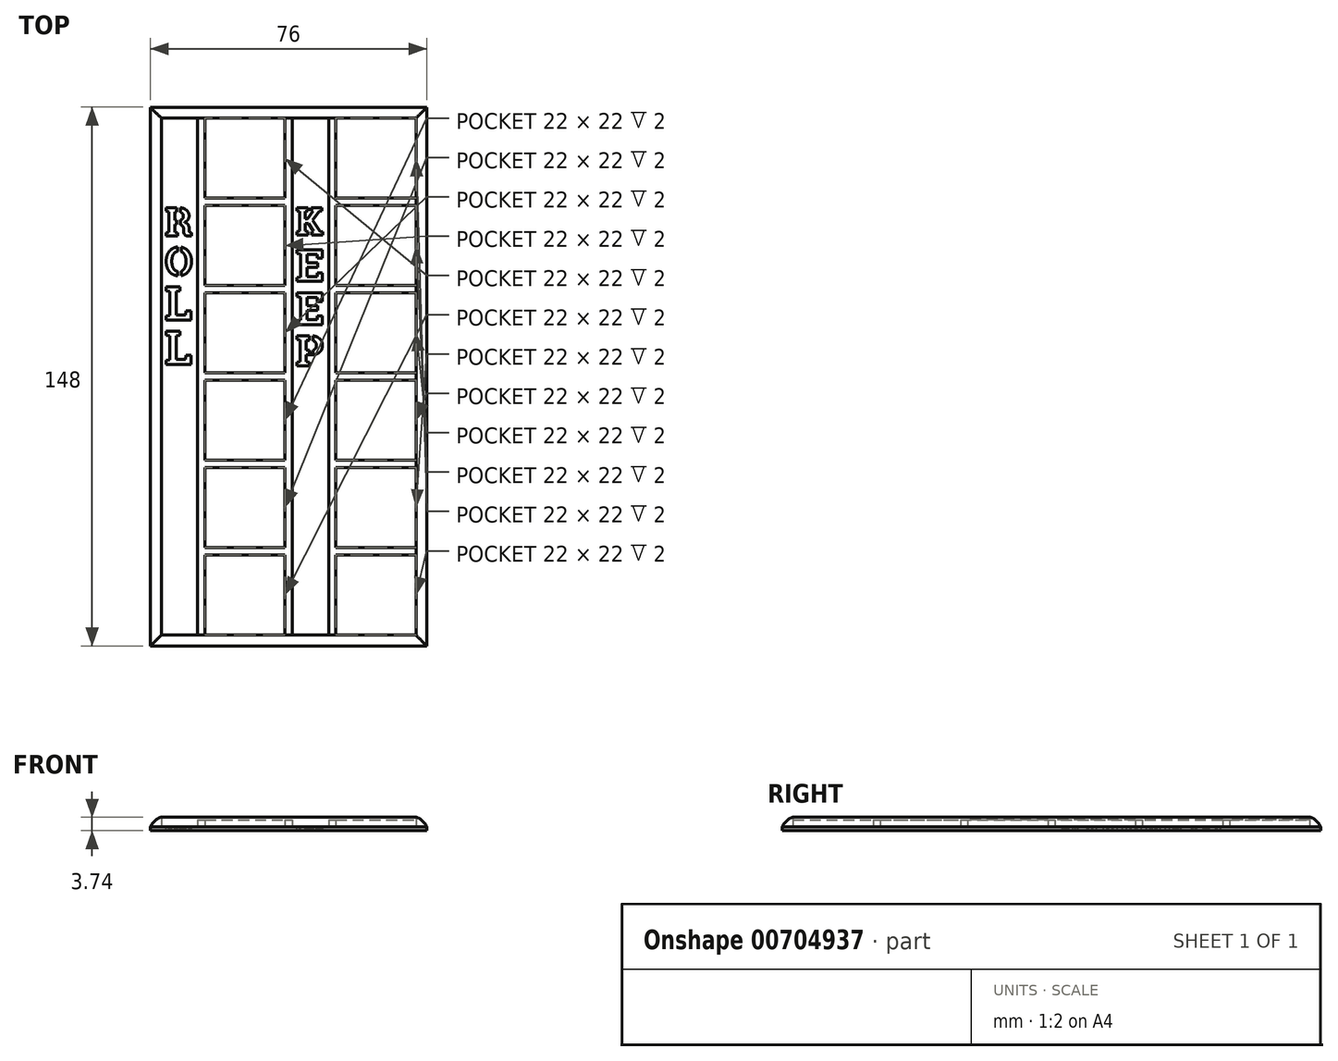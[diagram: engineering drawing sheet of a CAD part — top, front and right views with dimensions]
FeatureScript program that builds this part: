
annotation { "Feature Type Name" : "Feature", "Feature Type Description" : "" }
export const myFeature = defineFeature(function(context is Context, id is Id, definition is map)
    precondition{}
    {
        {
            var Q0;
            Q0=qCreatedBy(makeId("Top.planeOp"),FACE);
            var sketch = newSketch(context, id + "F0", { "sketchPlane" : qUnion([Q0])});
            skLineSegment(sketch, "E0.bottom", {"start": v(-38, 75.1) * mm, "end": v(38, 75.1) * mm});
            skLineSegment(sketch, "E0.top", {"start": v(-38, -72.9) * mm, "end": v(38, -72.9) * mm});
            skLineSegment(sketch, "E0.left", {"start": v(-38, 75.1) * mm, "end": v(-38, -72.9) * mm});
            skLineSegment(sketch, "E0.right", {"start": v(38, 75.1) * mm, "end": v(38, -72.9) * mm});
            skLineSegment(sketch, "E1.left", {"start": v(11, -69.9) * mm, "end": v(11, 72.1) * mm});
            skLineSegment(sketch, "E1.right", {"start": v(-35, -69.9) * mm, "end": v(-35, 72.1) * mm});
            skLineSegment(sketch, "E2", {"start": v(-25, 72.1) * mm, "end": v(-25, -69.9) * mm});
            skLineSegment(sketch, "E3.1.0.0", {"start": v(-1, 72.1) * mm, "end": v(-1, -69.9) * mm});
            skLineSegment(sketch, "E3.2.0.0", {"start": v(13, 72.1) * mm, "end": v(13, -69.9) * mm});
            skLineSegment(sketch, "E4", {"start": v(-23, -69.9) * mm, "end": v(-23, 72.1) * mm});
            skLineSegment(sketch, "E5.1.0.0", {"start": v(1, -69.9) * mm, "end": v(1, 72.1) * mm});
            skLineSegment(sketch, "E5.2.0.0", {"start": v(35, -69.9) * mm, "end": v(35, 72.1) * mm});
            skLineSegment(sketch, "E6", {"start": v(-35, 72.1) * mm, "end": v(35, 72.1) * mm});
            skLineSegment(sketch, "E7", {"start": v(35, -69.9) * mm, "end": v(-35, -69.9) * mm});
            skLineSegment(sketch, "E8.bottom", {"start": v(-29.5, 28.1) * mm, "end": v(-30.5, 28.1) * mm});
            skLineSegment(sketch, "E8.top", {"start": v(-29.5, 38.1) * mm, "end": v(-30.5, 38.1) * mm});
            skLineSegment(sketch, "E8.left", {"start": v(-29.5, 28.1) * mm, "end": v(-29.5, 38.1) * mm});
            skLineSegment(sketch, "E8.right", {"start": v(-30.5, 28.1) * mm, "end": v(-30.5, 38.1) * mm});
            skLineSegment(sketch, "E9.bottom", {"start": v(-30.75, 52.1) * mm, "end": v(-29.75, 52.1) * mm});
            skLineSegment(sketch, "E9.top", {"start": v(-30.75, 42.1) * mm, "end": v(-29.75, 42.1) * mm});
            skLineSegment(sketch, "E9.left", {"start": v(-30.75, 52.1) * mm, "end": v(-30.75, 42.1) * mm});
            skLineSegment(sketch, "E9.right", {"start": v(-29.75, 52.1) * mm, "end": v(-29.75, 42.1) * mm});
            skLineSegment(sketch, "E10.bottom", {"start": v(5.75, 7.6) * mm, "end": v(6.75, 7.6) * mm});
            skLineSegment(sketch, "E10.top", {"start": v(5.75, 13.6) * mm, "end": v(6.75, 13.6) * mm});
            skLineSegment(sketch, "E10.left", {"start": v(5.75, 7.6) * mm, "end": v(5.75, 13.6) * mm});
            skLineSegment(sketch, "E10.right", {"start": v(6.75, 7.6) * mm, "end": v(6.75, 13.6) * mm});
            skSolve(sketch);
        }
        {
            var Q0;
            Q0=qCreatedBy(makeId("Top.planeOp"),FACE);
            var sketch = newSketch(context, id + "F1", { "sketchPlane" : qUnion([Q0])});
            skLineSegment(sketch, "E11", {"start": v(-25, 72.1) * mm, "end": v(-25, -69.9) * mm});
            skLineSegment(sketch, "E12", {"start": v(-35, -69.9) * mm, "end": v(-35, 72.1) * mm});
            skLineSegment(sketch, "E13", {"start": v(11, -69.9) * mm, "end": v(11, 72.1) * mm});
            skLineSegment(sketch, "E14", {"start": v(13, 72.1) * mm, "end": v(13, -69.9) * mm});
            skLineSegment(sketch, "E15", {"start": v(-23, 72.1) * mm, "end": v(-1, 72.1) * mm});
            skLineSegment(sketch, "E16", {"start": v(-23, -69.9) * mm, "end": v(-23, 72.1) * mm});
            skLineSegment(sketch, "E17", {"start": v(-1, -69.9) * mm, "end": v(-23, -69.9) * mm});
            skLineSegment(sketch, "E18", {"start": v(-1, 72.1) * mm, "end": v(-1, -69.9) * mm});
            skLineSegment(sketch, "E19", {"start": v(-25, 72.1) * mm, "end": v(-23, 72.1) * mm});
            skLineSegment(sketch, "E20", {"start": v(-23, -69.9) * mm, "end": v(-25, -69.9) * mm});
            skLineSegment(sketch, "E21.bottom", {"start": v(-23, 50.1) * mm, "end": v(-1, 50.1) * mm});
            skLineSegment(sketch, "E21.top", {"start": v(-23, 48.1) * mm, "end": v(-1, 48.1) * mm});
            skLineSegment(sketch, "E21.left", {"start": v(-23, 50.1) * mm, "end": v(-23, 48.1) * mm});
            skLineSegment(sketch, "E21.right", {"start": v(-1, 50.1) * mm, "end": v(-1, 48.1) * mm});
            skLineSegment(sketch, "E22.bottom", {"start": v(-23, 26.1) * mm, "end": v(-1, 26.1) * mm});
            skLineSegment(sketch, "E22.top", {"start": v(-23, 24.1) * mm, "end": v(-1, 24.1) * mm});
            skLineSegment(sketch, "E23.bottom", {"start": v(-23, 2.1) * mm, "end": v(-1, 2.1) * mm});
            skLineSegment(sketch, "E23.top", {"start": v(-23, 0.1) * mm, "end": v(-1, 0.1) * mm});
            skLineSegment(sketch, "E24.bottom", {"start": v(-23, -21.9) * mm, "end": v(-1, -21.9) * mm});
            skLineSegment(sketch, "E24.top", {"start": v(-23, -23.9) * mm, "end": v(-1, -23.9) * mm});
            skLineSegment(sketch, "E25.bottom", {"start": v(-23, -45.9) * mm, "end": v(-1, -45.9) * mm});
            skLineSegment(sketch, "E25.top", {"start": v(-23, -47.9) * mm, "end": v(-1, -47.9) * mm});
            skLineSegment(sketch, "E26.bottom", {"start": v(13, 50.1) * mm, "end": v(35, 50.1) * mm});
            skLineSegment(sketch, "E26.top", {"start": v(13, 48.1) * mm, "end": v(35, 48.1) * mm});
            skLineSegment(sketch, "E27.bottom", {"start": v(13, 26.1) * mm, "end": v(35, 26.1) * mm});
            skLineSegment(sketch, "E27.top", {"start": v(13, 24.1) * mm, "end": v(35, 24.1) * mm});
            skLineSegment(sketch, "E28.bottom", {"start": v(13, 2.1) * mm, "end": v(35, 2.1) * mm});
            skLineSegment(sketch, "E28.top", {"start": v(13, 0.1) * mm, "end": v(35, 0.1) * mm});
            skLineSegment(sketch, "E29.bottom", {"start": v(13, -21.9) * mm, "end": v(35, -21.9) * mm});
            skLineSegment(sketch, "E29.top", {"start": v(13, -23.9) * mm, "end": v(35, -23.9) * mm});
            skLineSegment(sketch, "E30.bottom", {"start": v(13, -45.9) * mm, "end": v(35, -45.9) * mm});
            skLineSegment(sketch, "E30.top", {"start": v(13, -47.9) * mm, "end": v(35, -47.9) * mm});
            skLineSegment(sketch, "E31", {"start": v(13, -69.9) * mm, "end": v(11, -69.9) * mm});
            skLineSegment(sketch, "E32", {"start": v(11, 72.1) * mm, "end": v(13, 72.1) * mm});
            skLineSegment(sketch, "E33", {"start": v(35, -69.9) * mm, "end": v(13, -69.9) * mm});
            skLineSegment(sketch, "E34", {"start": v(35, -69.9) * mm, "end": v(35, 72.1) * mm});
            skLineSegment(sketch, "E35", {"start": v(13, 72.1) * mm, "end": v(35, 72.1) * mm});
            skSolve(sketch);
        }
        {
            var Q0;
            Q0=makeQuery(id+"F0.imprint","IMPRINT",FACE,{"disambiguationData":[TD([[makeQuery(id+"F0.imprint","IMPRINT",EDGE,{"derivedFrom":sQuery(id+"F0.wireOp",EDGE,"E0.bottom")}),-1.0]])]});
            var Q1;
            Q1=sQuery(id+"F0.wireOp",EDGE,"E1.top");
            var Q2;
            Q2=sQuery(id+"F1.wireOp",EDGE,"1024a238-9103-462a-9477-26902ec0aa7303");
            var Q3;
            Q3=sQuery(id+"F0.wireOp",EDGE,"E0.bottom");
            var Q4;
            Q4=sQuery(id+"F0.wireOp",EDGE,"E1.right");
            var Q5;
            Q5=sQuery(id+"F0.wireOp",EDGE,"E0.left");
            var Q6;
            Q6=sQuery(id+"F0.wireOp",EDGE,"E0.top");
            var Q7;
            Q7=sQuery(id+"F0.wireOp",EDGE,"E1.bottom");
            var Q8;
            Q8=sQuery(id+"F1.wireOp",EDGE,"1024a238-9103-462a-9477-26902ec0aa7301");
            var Q9;
            Q9=sQuery(id+"F0.wireOp",EDGE,"E1.left");
            var Q10;
            Q10=sQuery(id+"F0.wireOp",EDGE,"E0.right");
            extrude(context, id + "F2", {"entities" : qUnion([Q0]), "surfaceEntities" : qUnion([Q1, Q2, Q3, Q4, Q5, Q6, Q7, Q8, Q9, Q10]), "depth" : 3 * mm, "offsetDistance" : 25 * mm});
        }
        {
            var Q0;
            {var subQ0=sQuery(id+"F0.wireOp",EDGE,"E2");Q0=makeQuery(id+"F0.imprint","IMPRINT",FACE,{"disambiguationData":[TD([[makeQuery(id+"F0.imprint","IMPRINT",EDGE,{"derivedFrom":subQ0}),1.0]])]});}
            var Q1;
            {var subQ0=sQuery(id+"F0.wireOp",EDGE,"E3.1.0.0");Q1=makeQuery(id+"F0.imprint","IMPRINT",FACE,{"disambiguationData":[TD([[makeQuery(id+"F0.imprint","IMPRINT",EDGE,{"derivedFrom":subQ0}),1.0]])]});}
            var Q2;
            {var subQ0=sQuery(id+"F0.wireOp",EDGE,"E1.left");Q2=makeQuery(id+"F0.imprint","IMPRINT",FACE,{"disambiguationData":[TD([[makeQuery(id+"F0.imprint","IMPRINT",EDGE,{"derivedFrom":subQ0}),-1.0]])]});}
            var Q3;
            Q3=sQuery(id+"F0.wireOp",EDGE,"E2");
            var Q4;
            Q4=sQuery(id+"F0.wireOp",EDGE,"E4");
            extrude(context, id + "F3", {"entities" : qUnion([Q0, Q1, Q2]), "operationType" : NewBodyOperationType.ADD, "surfaceEntities" : qUnion([Q3, Q4]), "depth" : 2 * mm, "offsetDistance" : 25 * mm});
        }
        {
            var Q0;
            Q0=makeQuery(id+"F2.opExtrude","CAP_EDGE",EDGE,{"disambiguationData":[OSD([sQuery(id+"F0.wireOp",EDGE,"E0.right")])],"isStart":false});
            var Q1;
            Q1=makeQuery(id+"F2.opExtrude","CAP_EDGE",EDGE,{"disambiguationData":[OSD([sQuery(id+"F0.wireOp",EDGE,"E0.top")])],"isStart":false});
            var Q2;
            Q2=makeQuery(id+"F2.opExtrude","CAP_EDGE",EDGE,{"disambiguationData":[OSD([sQuery(id+"F0.wireOp",EDGE,"E0.left")])],"isStart":false});
            var Q3;
            Q3=makeQuery(id+"F2.opExtrude","CAP_EDGE",EDGE,{"disambiguationData":[OSD([sQuery(id+"F0.wireOp",EDGE,"E0.bottom")])],"isStart":false});
            fillet(context, id + "F4", {"entities" : qUnion([Q0, Q1, Q2, Q3]), "radius" : 5 * mm, "tangentPropagation" : true, "allowEdgeOverflow" : false});
        }
        {
            var Q0;
            Q0=qCreatedBy(makeId("Top.planeOp"),FACE);
            var sketch = newSketch(context, id + "F5", { "sketchPlane" : qUnion([Q0])});
            skLineSegment(sketch, "E36.bottom", {"start": v(-38, -72.9) * mm, "end": v(38, -72.9) * mm});
            skLineSegment(sketch, "E36.top", {"start": v(-38, 75.1) * mm, "end": v(38, 75.1) * mm});
            skLineSegment(sketch, "E36.left", {"start": v(-38, -72.9) * mm, "end": v(-38, 75.1) * mm});
            skLineSegment(sketch, "E36.right", {"start": v(38, -72.9) * mm, "end": v(38, 75.1) * mm});
            skSolve(sketch);
        }
        {
            var Q0;
            {var subQ0=sQuery(id+"F1.wireOp",EDGE,"E26.bottom");Q0=makeQuery(id+"F1.imprint","IMPRINT",FACE,{"disambiguationData":[TD([[makeQuery(id+"F1.imprint","IMPRINT",EDGE,{"derivedFrom":subQ0}),-1.0]])]});}
            var Q1;
            {var subQ0=sQuery(id+"F1.wireOp",EDGE,"E27.bottom");Q1=makeQuery(id+"F1.imprint","IMPRINT",FACE,{"disambiguationData":[TD([[makeQuery(id+"F1.imprint","IMPRINT",EDGE,{"derivedFrom":subQ0}),-1.0]])]});}
            var Q2;
            {var subQ0=sQuery(id+"F1.wireOp",EDGE,"E28.bottom");Q2=makeQuery(id+"F1.imprint","IMPRINT",FACE,{"disambiguationData":[TD([[makeQuery(id+"F1.imprint","IMPRINT",EDGE,{"derivedFrom":subQ0}),-1.0]])]});}
            var Q3;
            {var subQ0=sQuery(id+"F1.wireOp",EDGE,"E29.bottom");Q3=makeQuery(id+"F1.imprint","IMPRINT",FACE,{"disambiguationData":[TD([[makeQuery(id+"F1.imprint","IMPRINT",EDGE,{"derivedFrom":subQ0}),-1.0]])]});}
            var Q4;
            {var subQ0=sQuery(id+"F1.wireOp",EDGE,"E30.bottom");Q4=makeQuery(id+"F1.imprint","IMPRINT",FACE,{"disambiguationData":[TD([[makeQuery(id+"F1.imprint","IMPRINT",EDGE,{"derivedFrom":subQ0}),-1.0]])]});}
            var Q5;
            {var subQ0=sQuery(id+"F1.wireOp",EDGE,"E25.bottom");Q5=makeQuery(id+"F1.imprint","IMPRINT",FACE,{"disambiguationData":[TD([[makeQuery(id+"F1.imprint","IMPRINT",EDGE,{"derivedFrom":subQ0}),-1.0]])]});}
            var Q6;
            {var subQ0=sQuery(id+"F1.wireOp",EDGE,"E24.bottom");Q6=makeQuery(id+"F1.imprint","IMPRINT",FACE,{"disambiguationData":[TD([[makeQuery(id+"F1.imprint","IMPRINT",EDGE,{"derivedFrom":subQ0}),-1.0]])]});}
            var Q7;
            {var subQ0=sQuery(id+"F1.wireOp",EDGE,"E23.bottom");Q7=makeQuery(id+"F1.imprint","IMPRINT",FACE,{"disambiguationData":[TD([[makeQuery(id+"F1.imprint","IMPRINT",EDGE,{"derivedFrom":subQ0}),-1.0]])]});}
            var Q8;
            {var subQ0=sQuery(id+"F1.wireOp",EDGE,"E22.bottom");Q8=makeQuery(id+"F1.imprint","IMPRINT",FACE,{"disambiguationData":[TD([[makeQuery(id+"F1.imprint","IMPRINT",EDGE,{"derivedFrom":subQ0}),-1.0]])]});}
            var Q9;
            Q9=makeQuery(id+"F1.imprint","IMPRINT",FACE,{"disambiguationData":[TD([[makeQuery(id+"F1.imprint","IMPRINT",EDGE,{"derivedFrom":sQuery(id+"F1.wireOp",EDGE,"E21.bottom")}),-1.0]])]});
            extrude(context, id + "F6", {"entities" : qUnion([Q0, Q1, Q2, Q3, Q4, Q5, Q6, Q7, Q8, Q9]), "operationType" : NewBodyOperationType.ADD, "depth" : 2 * mm, "offsetDistance" : 25 * mm});
        }
        {
            var Q0;
            Q0=qCreatedBy(makeId("Top.planeOp"),FACE);
            var sketch = newSketch(context, id + "F7", { "sketchPlane" : qUnion([Q0])});
            skText(sketch, "E37", { "text": "R", "fontName": "RobotoSlab-Bold.ttf"});
            const initialGuessF7  = {"E37": [-0.034, 0.0397, 1, 0, 0.0079]};
            skSetInitialGuess(sketch, initialGuessF7);
            skSolve(sketch);
        }
        {
            var Q0;
            Q0=qCreatedBy(makeId("Top.planeOp"),FACE);
            var sketch = newSketch(context, id + "F8", { "sketchPlane" : qUnion([Q0])});
            skText(sketch, "E38", { "text": "O", "fontName": "RobotoSlab-Bold.ttf"});
            const initialGuessF8  = {"E38": [-0.034, 0.0289, 1, 0, 0.0078], "E38": [-0.034, 0.0289, 1, 0, 0.0078]};
            skSetInitialGuess(sketch, initialGuessF8);
            skSolve(sketch);
        }
        {
            var Q0;
            Q0=qCreatedBy(makeId("Top.planeOp"),FACE);
            var sketch = newSketch(context, id + "F9", { "sketchPlane" : qUnion([Q0])});
            skText(sketch, "E39", { "text": "L", "fontName": "RobotoSlab-Bold.ttf"});
            const initialGuessF9  = {"E39": [-0.034, 0.01666, 1, 0, 0.00924]};
            skSetInitialGuess(sketch, initialGuessF9);
            skSolve(sketch);
        }
        {
            var Q0;
            Q0=qCreatedBy(makeId("Top.planeOp"),FACE);
            var sketch = newSketch(context, id + "F10", { "sketchPlane" : qUnion([Q0])});
            skText(sketch, "E40", { "text": "L", "fontName": "RobotoSlab-Bold.ttf"});
            const initialGuessF10  = {"E40": [-0.034, 0.00442, 1, 0, 0.00924]};
            skSetInitialGuess(sketch, initialGuessF10);
            skSolve(sketch);
        }
        {
            var Q0;
            Q0=qCreatedBy(makeId("Top.planeOp"),FACE);
            var sketch = newSketch(context, id + "F11", { "sketchPlane" : qUnion([Q0])});
            skText(sketch, "E41", { "text": "K", "fontName": "RobotoSlab-Bold.ttf"});
            const initialGuessF11  = {"E41": [0.002, 0.04004, 1, 0, 0.00757]};
            skSetInitialGuess(sketch, initialGuessF11);
            skSolve(sketch);
        }
        {
            var Q0;
            Q0=qCreatedBy(makeId("Top.planeOp"),FACE);
            var sketch = newSketch(context, id + "F12", { "sketchPlane" : qUnion([Q0])});
            skText(sketch, "E42", { "text": "E", "fontName": "RobotoSlab-Bold.ttf"});
            const initialGuessF12  = {"E42": [0.002, 0.02724, 1, 0, 0.00885]};
            skSetInitialGuess(sketch, initialGuessF12);
            skSolve(sketch);
        }
        {
            var Q0;
            Q0=qCreatedBy(makeId("Top.planeOp"),FACE);
            var sketch = newSketch(context, id + "F13", { "sketchPlane" : qUnion([Q0])});
            skText(sketch, "E43", { "text": "E", "fontName": "RobotoSlab-Bold.ttf"});
            const initialGuessF13  = {"E43": [0.002, 0.0154, 1, 0, 0.00885]};
            skSetInitialGuess(sketch, initialGuessF13);
            skSolve(sketch);
        }
        {
            var Q0;
            Q0=qCreatedBy(makeId("Top.planeOp"),FACE);
            var sketch = newSketch(context, id + "F14", { "sketchPlane" : qUnion([Q0])});
            skText(sketch, "E44", { "text": "P", "fontName": "RobotoSlab-Bold.ttf"});
            const initialGuessF14  = {"E44": [0.002, 0.00405, 1, 0, 0.00835]};
            skSetInitialGuess(sketch, initialGuessF14);
            skSolve(sketch);
        }
        {
            var Q0;
            Q0 = qSketchRegion(id + "F5", true);
            extrude(context, id + "F15", {"entities" : qUnion([Q0]), "operationType" : NewBodyOperationType.ADD, "oppositeDirection" : true, "depth" : 1 * mm, "offsetDistance" : 25 * mm});
        }
        {
            var Q0;
            Q0 = qSketchRegion(id + "F14", true);
            var Q1;
            Q1 = qSketchRegion(id + "F11", true);
            var Q2;
            Q2 = qSketchRegion(id + "F12", true);
            var Q3;
            Q3 = qSketchRegion(id + "F9", true);
            var Q4;
            Q4 = qSketchRegion(id + "F10", true);
            var Q5;
            Q5 = qSketchRegion(id + "F7", true);
            var Q6;
            Q6 = qSketchRegion(id + "F8", true);
            var Q7;
            Q7 = qSketchRegion(id + "F13", true);
            extrude(context, id + "F16", {"entities" : qUnion([Q0, Q1, Q2, Q3, Q4, Q5, Q6, Q7]), "operationType" : NewBodyOperationType.REMOVE, "oppositeDirection" : true, "depth" : 10 * mm, "offsetDistance" : 25 * mm});
        }
        {
            var Q0;
            Q0=makeQuery(id+"F0.imprint","IMPRINT",FACE,{"disambiguationData":[TD([[makeQuery(id+"F0.imprint","IMPRINT",EDGE,{"derivedFrom":sQuery(id+"F0.wireOp",EDGE,"E8.bottom")}),-1.0]])]});
            extrude(context, id + "F17", {"entities" : qUnion([Q0]), "operationType" : NewBodyOperationType.ADD, "oppositeDirection" : true, "depth" : 1 * mm, "offsetDistance" : 25 * mm});
        }
        {
            var Q0;
            Q0=makeQuery(id+"F0.imprint","IMPRINT",FACE,{"disambiguationData":[TD([[makeQuery(id+"F0.imprint","IMPRINT",EDGE,{"derivedFrom":sQuery(id+"F0.wireOp",EDGE,"E9.bottom")}),-1.0]])]});
            extrude(context, id + "F18", {"entities" : qUnion([Q0]), "operationType" : NewBodyOperationType.ADD, "oppositeDirection" : true, "depth" : 1 * mm, "offsetDistance" : 25 * mm});
        }
        {
            var Q0;
            Q0=makeQuery(id+"F0.imprint","IMPRINT",FACE,{"disambiguationData":[TD([[makeQuery(id+"F0.imprint","IMPRINT",EDGE,{"derivedFrom":sQuery(id+"F0.wireOp",EDGE,"E10.bottom")}),1.0]])]});
            extrude(context, id + "F19", {"entities" : qUnion([Q0]), "operationType" : NewBodyOperationType.ADD, "oppositeDirection" : true, "depth" : 1 * mm, "offsetDistance" : 25 * mm});
        }
    });
